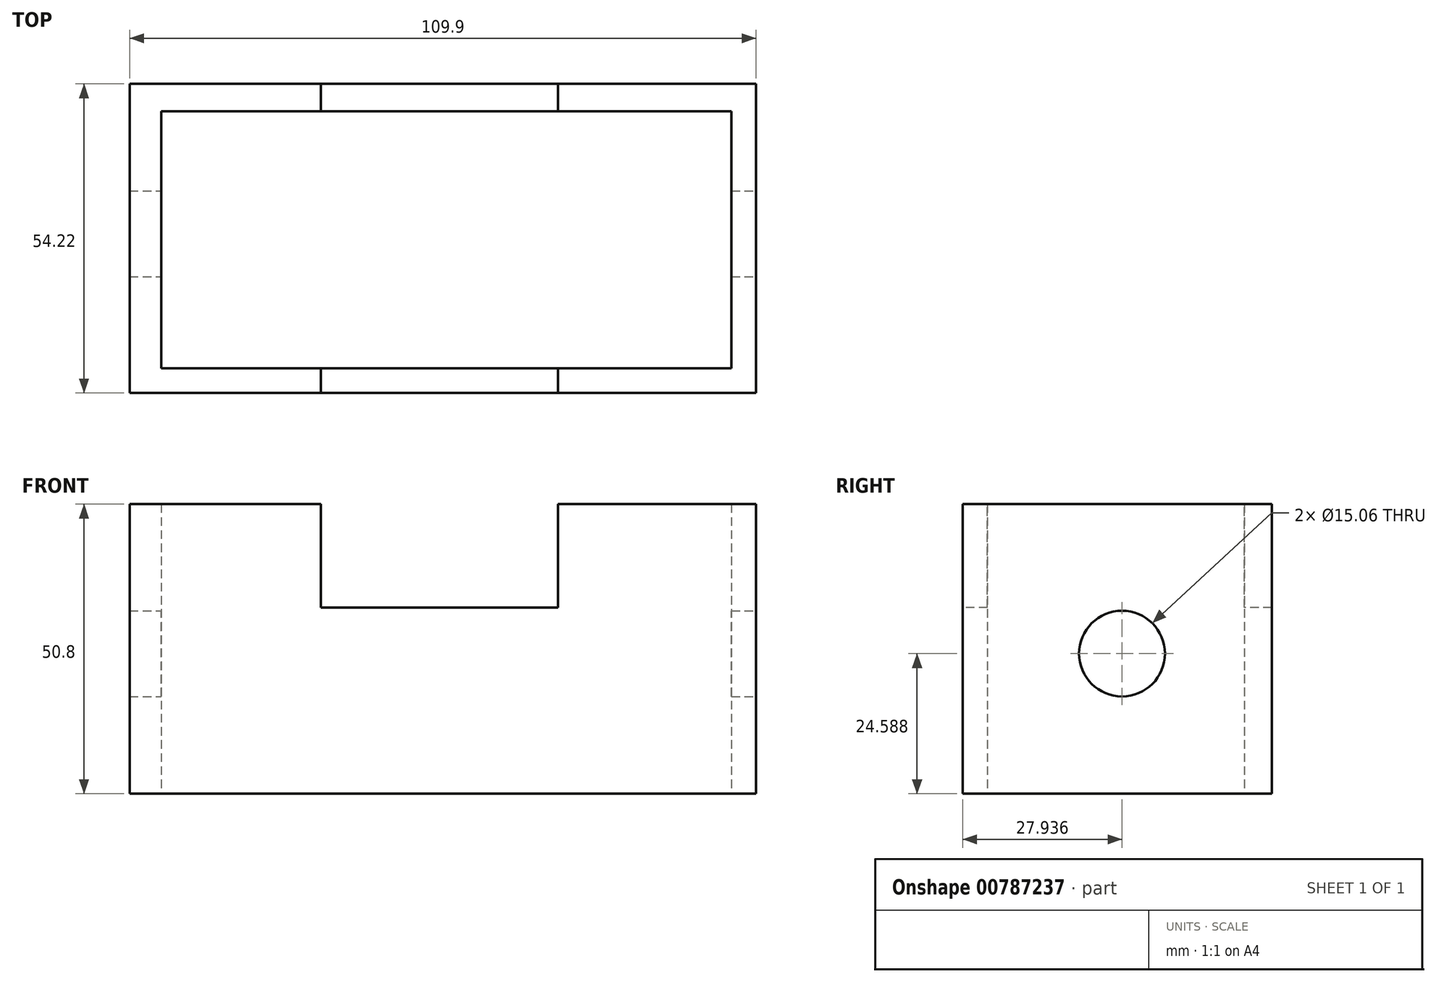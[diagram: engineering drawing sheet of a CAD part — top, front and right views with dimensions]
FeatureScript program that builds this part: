
annotation { "Feature Type Name" : "Feature", "Feature Type Description" : "" }
export const myFeature = defineFeature(function(context is Context, id is Id, definition is map)
    precondition{}
    {
        {
            var Q0;
            Q0=qCreatedBy(makeId("Top.planeOp"),FACE);
            var sketch = newSketch(context, id + "F0", { "sketchPlane" : qUnion([Q0])});
            skLineSegment(sketch, "E0.bottom", {"start": v(-50.49, 43.74) * mm, "end": v(59.4, 43.74) * mm});
            skLineSegment(sketch, "E0.top", {"start": v(-50.49, -10.48) * mm, "end": v(59.4, -10.48) * mm});
            skLineSegment(sketch, "E0.left", {"start": v(-50.49, 43.74) * mm, "end": v(-50.49, -10.48) * mm});
            skLineSegment(sketch, "E0.right", {"start": v(59.4, 43.74) * mm, "end": v(59.4, -10.48) * mm});
            skLineSegment(sketch, "E1.bottom", {"start": v(-44.95, 38.92) * mm, "end": v(55.07, 38.92) * mm});
            skLineSegment(sketch, "E1.top", {"start": v(-44.95, -6.15) * mm, "end": v(55.07, -6.15) * mm});
            skLineSegment(sketch, "E1.left", {"start": v(-44.95, 38.92) * mm, "end": v(-44.95, -6.15) * mm});
            skLineSegment(sketch, "E1.right", {"start": v(55.07, 38.92) * mm, "end": v(55.07, -6.15) * mm});
            skSolve(sketch);
        }
        {
            var Q0;
            Q0=makeQuery(id+"F0.imprint","IMPRINT",FACE,{"disambiguationData":[TD([[makeQuery(id+"F0.imprint","IMPRINT",EDGE,{"derivedFrom":sQuery(id+"F0.wireOp",EDGE,"E0.bottom")}),-1.0]])]});
            extrude(context, id + "F1", {"entities" : qUnion([Q0]), "depth" : 50.8 * mm, "offsetDistance" : 25.4 * mm});
        }
        {
            var Q0;
            Q0=makeQuery(id+"F1.opExtrude","SWEPT_FACE",FACE,{"disambiguationData":[OSD([sQuery(id+"F0.wireOp",EDGE,"E0.top")])]});
            var sketch = newSketch(context, id + "F2", { "sketchPlane" : qUnion([Q0])});
            skLineSegment(sketch, "E2.bottom", {"start": v(-16.94, 50.8) * mm, "end": v(24.63, 50.8) * mm});
            skLineSegment(sketch, "E2.top", {"start": v(-16.94, 32.63) * mm, "end": v(24.63, 32.63) * mm});
            skLineSegment(sketch, "E2.left", {"start": v(-16.94, 50.8) * mm, "end": v(-16.94, 32.63) * mm});
            skLineSegment(sketch, "E2.right", {"start": v(24.63, 50.8) * mm, "end": v(24.63, 32.63) * mm});
            skSolve(sketch);
        }
        {
            var Q0;
            Q0=makeQuery(id+"F1.opExtrude","SWEPT_FACE",FACE,{"disambiguationData":[OSD([sQuery(id+"F0.wireOp",EDGE,"E0.right")])]});
            var sketch = newSketch(context, id + "F3", { "sketchPlane" : qUnion([Q0])});
            skCircle(sketch, "E3", {"center": v(17.46, 24.59) * mm, "radius": 7.53 * mm});
            skSolve(sketch);
        }
        {
            var Q0;
            Q0=makeQuery(id+"F2.imprint","IMPRINT",FACE,{"disambiguationData":[TD([[makeQuery(id+"F2.imprint","IMPRINT",EDGE,{"derivedFrom":sQuery(id+"F2.wireOp",EDGE,"E2.bottom")}),-1.0]])]});
            extrude(context, id + "F4", {"entities" : qUnion([Q0]), "operationType" : NewBodyOperationType.REMOVE, "oppositeDirection" : true, "depth" : 70.61 * mm, "offsetDistance" : 25.4 * mm});
        }
        {
            var Q0;
            Q0=makeQuery(id+"F3.imprint","IMPRINT",FACE,{"disambiguationData":[TD([[makeQuery(id+"F3.imprint","IMPRINT",EDGE,{"derivedFrom":sQuery(id+"F3.wireOp",EDGE,"E3")}),1.0]])]});
            extrude(context, id + "F5", {"entities" : qUnion([Q0]), "operationType" : NewBodyOperationType.REMOVE, "oppositeDirection" : true, "depth" : 124.7 * mm, "offsetDistance" : 25.4 * mm});
        }
    });
